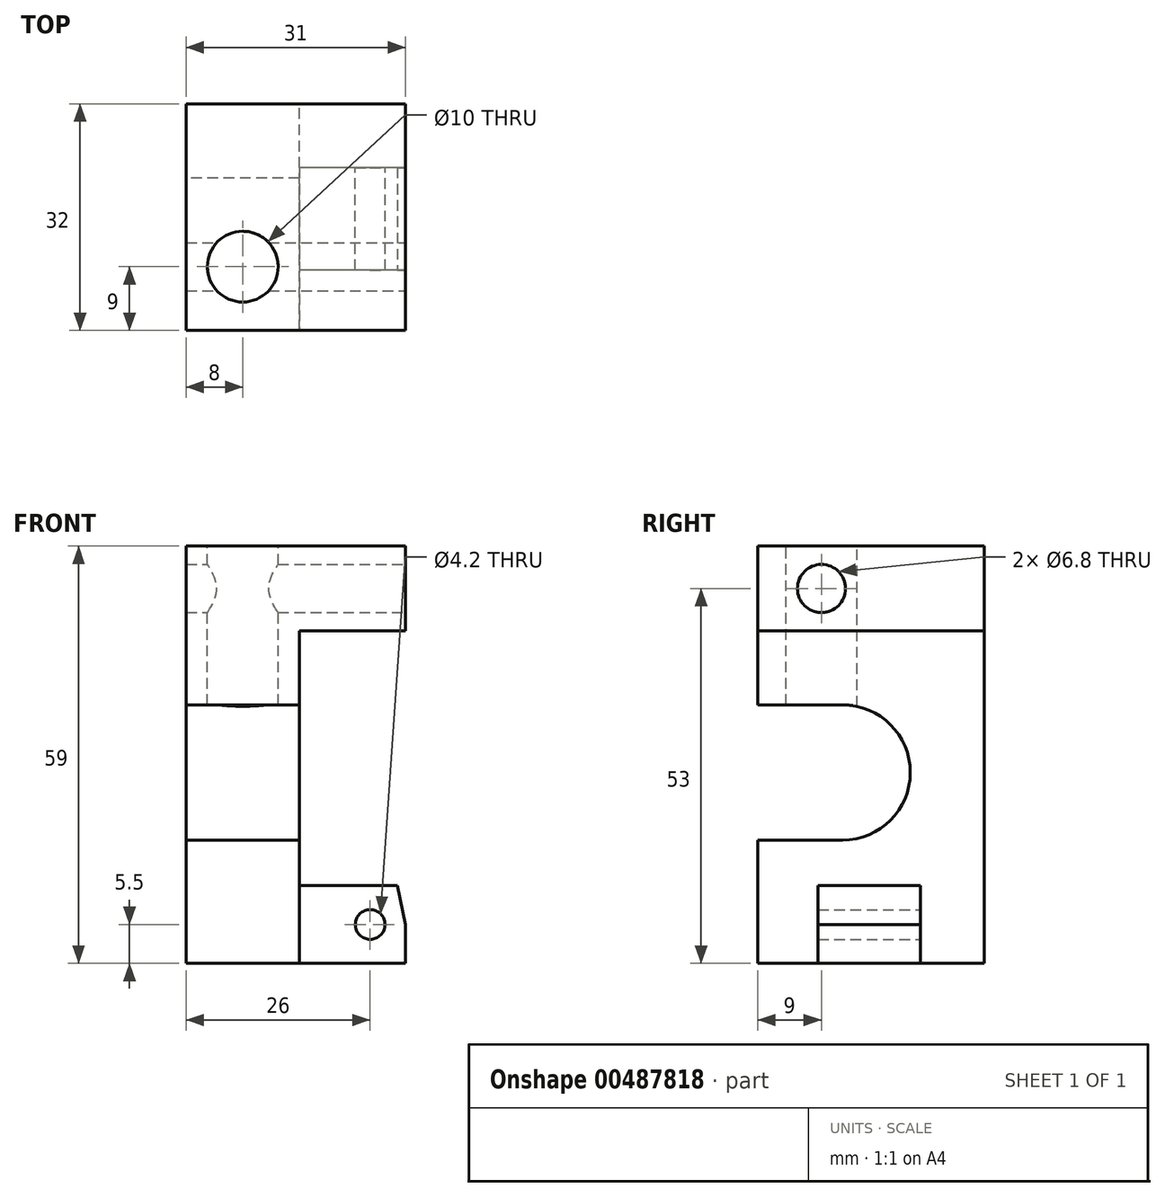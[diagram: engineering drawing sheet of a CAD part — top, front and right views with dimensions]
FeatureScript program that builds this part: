
annotation { "Feature Type Name" : "Feature", "Feature Type Description" : "" }
export const myFeature = defineFeature(function(context is Context, id is Id, definition is map)
    precondition{}
    {
        {
            var Q0;
            Q0=qCreatedBy(makeId("Right.planeOp"),FACE);
            var sketch = newSketch(context, id + "F0", { "sketchPlane" : qUnion([Q0])});
            skArc(sketch, "E0", {"start": v(0, -9.55) * mm, "mid": v(9.55, 0) * mm, "end": v(0, 9.55) * mm});
            skLineSegment(sketch, "E1.bottom", {"start": v(-12, 32) * mm, "end": v(20, 32) * mm});
            skLineSegment(sketch, "E1.top", {"start": v(-12, -27) * mm, "end": v(20, -27) * mm});
            skLineSegment(sketch, "E1.left", {"start": v(-12, 32) * mm, "end": v(-12, -27) * mm});
            skLineSegment(sketch, "E1.right", {"start": v(20, 32) * mm, "end": v(20, -27) * mm});
            skLineSegment(sketch, "E2.bottom", {"start": v(0, 9.55) * mm, "end": v(-12, 9.55) * mm});
            skLineSegment(sketch, "E2.top", {"start": v(0, -9.55) * mm, "end": v(-12, -9.55) * mm});
            skPoint(sketch, "E3.orphan", {"position": v(20, 9.55) * mm});
            skPoint(sketch, "E4.orphan", {"position": v(20, -9.55) * mm});
            skPoint(sketch, "E2.right.start.orphan", {"position": v(-20, 9.55) * mm});
            skPoint(sketch, "E5.orphan", {"position": v(-20, -9.55) * mm});
            skSolve(sketch);
        }
        {
            var Q0;
            Q0=makeQuery(id+"F0.imprint","IMPRINT",FACE,{"disambiguationData":[TD([[makeQuery(id+"F0.imprint","IMPRINT",EDGE,{"derivedFrom":sQuery(id+"F0.wireOp",EDGE,"E0")}),-1.0]])]});
            extrude(context, id + "F1", {"entities" : qUnion([Q0]), "depth" : 16 * mm, "offsetDistance" : 25 * mm});
        }
        {
            var Q0;
            Q0=makeQuery(id+"F1.opExtrude","CAP_FACE",FACE,{"disambiguationData":[OSD([sQuery(id+"F0.wireOp",EDGE,"E0"),sQuery(id+"F0.wireOp",EDGE,"E1.bottom"),sQuery(id+"F0.wireOp",EDGE,"E1.top"),sQuery(id+"F0.wireOp",EDGE,"E1.left"),sQuery(id+"F0.wireOp",EDGE,"E1.right")])],"isStart":false});
            var sketch = newSketch(context, id + "F2", { "sketchPlane" : qUnion([Q0])});
            skLineSegment(sketch, "E6.bottom", {"start": v(11, -27) * mm, "end": v(-3.5, -27) * mm});
            skLineSegment(sketch, "E6.top", {"start": v(11, -16) * mm, "end": v(-3.5, -16) * mm});
            skLineSegment(sketch, "E6.left", {"start": v(11, -27) * mm, "end": v(11, -16) * mm});
            skLineSegment(sketch, "E6.right", {"start": v(-3.5, -27) * mm, "end": v(-3.5, -16) * mm});
            skSolve(sketch);
        }
        {
            var Q0;
            Q0=makeQuery(id+"F2.imprint","IMPRINT",FACE,{"disambiguationData":[TD([[makeQuery(id+"F2.imprint","IMPRINT",EDGE,{"derivedFrom":sQuery(id+"F2.wireOp",EDGE,"E6.bottom")}),1.0]])]});
            extrude(context, id + "F3", {"entities" : qUnion([Q0]), "operationType" : NewBodyOperationType.ADD, "depth" : 15 * mm, "offsetDistance" : 25 * mm});
        }
        {
            var Q0;
            Q0=makeQuery(id+"F3.opExtrude","SWEPT_FACE",FACE,{"disambiguationData":[OSD([sQuery(id+"F2.wireOp",EDGE,"E6.right")])]});
            var sketch = newSketch(context, id + "F4", { "sketchPlane" : qUnion([Q0])});
            skLineSegment(sketch, "E7", {"start": v(31, -21.5) * mm, "end": v(31, -16) * mm});
            skLineSegment(sketch, "E8", {"start": v(31, -16) * mm, "end": v(29.83, -16) * mm});
            skLineSegment(sketch, "E9", {"start": v(29.83, -16) * mm, "end": v(31, -21.5) * mm});
            skSolve(sketch);
        }
        {
            var Q0;
            Q0=makeQuery(id+"F4.imprint","IMPRINT",FACE,{"disambiguationData":[TD([[makeQuery(id+"F4.imprint","IMPRINT",EDGE,{"derivedFrom":sQuery(id+"F4.wireOp",EDGE,"E7")}),1.0]])]});
            extrude(context, id + "F5", {"entities" : qUnion([Q0]), "operationType" : NewBodyOperationType.REMOVE, "endBound" : BoundingType.THROUGH_ALL, "oppositeDirection" : true, "depth" : 25 * mm, "offsetDistance" : 25 * mm});
        }
        {
            var Q0;
            Q0=makeQuery(id+"F3.opExtrude","SWEPT_FACE",FACE,{"disambiguationData":[OSD([sQuery(id+"F2.wireOp",EDGE,"E6.left")])]});
            var sketch = newSketch(context, id + "F6", { "sketchPlane" : qUnion([Q0])});
            skPoint(sketch, "E10", {"position": v(-26, -21.5) * mm});
            skSolve(sketch);
        }
        {
            var Q0;
            Q0=sQuery(id+"F6.wireOp",VERTEX,"E10");
            var Q1;
            Q1=makeQuery(id+"F1.opExtrude","SWEPT_BODY",BODY,{"disambiguationData":[OSD([sQuery(id+"F0.wireOp",EDGE,"E0"),sQuery(id+"F0.wireOp",EDGE,"E1.bottom"),sQuery(id+"F0.wireOp",EDGE,"E1.top"),sQuery(id+"F0.wireOp",EDGE,"E1.left"),sQuery(id+"F0.wireOp",EDGE,"E1.right"),sQuery(id+"F0.wireOp",EDGE,"E2.bottom"),sQuery(id+"F0.wireOp",EDGE,"E2.top")])]});
            hole(context, id + "F7", {"style" : HoleStyle.SIMPLE, "endStyle" : HoleEndStyle.THROUGH, "standardTappedOrClearance" : lookupTablePath({ "standard" : "ISO", "engagement" : "75%", "pitch" : "0.8 mm", "size" : "M5", "type" : "Tapped" }), "standardBlindInLast" : lookupTablePath({ "standard" : "ISO", "engagement" : "75%", "pitch" : "0.8 mm", "size" : "M5", "type" : "Tapped" }), "holeDiameter" : 4.2 * mm, "showTappedDepth" : true, "isTappedThrough" : true, "tappedDepth" : 12 * mm, "tapClearance" : 3, "locations" : qUnion([Q0]), "scope" : qUnion([Q1]), "majorDiameter" : 5 * mm});
        }
        {
            var Q0;
            Q0=makeQuery(id+"F1.opExtrude","CAP_FACE",FACE,{"disambiguationData":[OSD([sQuery(id+"F0.wireOp",EDGE,"E0"),sQuery(id+"F0.wireOp",EDGE,"E1.bottom"),sQuery(id+"F0.wireOp",EDGE,"E1.top"),sQuery(id+"F0.wireOp",EDGE,"E1.left"),sQuery(id+"F0.wireOp",EDGE,"E1.right"),sQuery(id+"F0.wireOp",EDGE,"E2.bottom"),sQuery(id+"F0.wireOp",EDGE,"E2.top")])],"isStart":false});
            var sketch = newSketch(context, id + "F8", { "sketchPlane" : qUnion([Q0])});
            skLineSegment(sketch, "E11.bottom", {"start": v(-12, 32) * mm, "end": v(20, 32) * mm});
            skLineSegment(sketch, "E11.top", {"start": v(-12, 20) * mm, "end": v(20, 20) * mm});
            skLineSegment(sketch, "E11.left", {"start": v(-12, 32) * mm, "end": v(-12, 20) * mm});
            skLineSegment(sketch, "E11.right", {"start": v(20, 32) * mm, "end": v(20, 20) * mm});
            skSolve(sketch);
        }
        {
            var Q0;
            Q0=makeQuery(id+"F8.imprint","IMPRINT",FACE,{"disambiguationData":[TD([[makeQuery(id+"F8.imprint","IMPRINT",EDGE,{"derivedFrom":sQuery(id+"F8.wireOp",EDGE,"E11.bottom")}),-1.0]])]});
            extrude(context, id + "F9", {"entities" : qUnion([Q0]), "operationType" : NewBodyOperationType.ADD, "depth" : 15 * mm, "offsetDistance" : 25 * mm});
        }
        {
            var Q0;
            Q0=makeQuery(id+"F9.boolean.opBoolean","MERGE",FACE,{"derivedFrom":[makeQuery(id+"F1.opExtrude","SWEPT_FACE",FACE,{"disambiguationData":[OSD([sQuery(id+"F0.wireOp",EDGE,"E1.bottom")])]}),makeQuery(id+"F9.opExtrude","SWEPT_FACE",FACE,{"disambiguationData":[OSD([sQuery(id+"F8.wireOp",EDGE,"E11.bottom")])]})]});
            var sketch = newSketch(context, id + "F10", { "sketchPlane" : qUnion([Q0])});
            skCircle(sketch, "E12", {"center": v(8, -3) * mm, "radius": 5 * mm});
            skSolve(sketch);
        }
        {
            var Q0;
            Q0=makeQuery(id+"F10.imprint","IMPRINT",FACE,{"disambiguationData":[TD([[makeQuery(id+"F10.imprint","IMPRINT",EDGE,{"derivedFrom":sQuery(id+"F10.wireOp",EDGE,"E12")}),1.0]])]});
            extrude(context, id + "F11", {"entities" : qUnion([Q0]), "operationType" : NewBodyOperationType.REMOVE, "oppositeDirection" : true, "depth" : 25 * mm, "offsetDistance" : 25 * mm});
        }
        {
            var Q0;
            Q0=makeQuery(id+"F9.opExtrude","CAP_FACE",FACE,{"disambiguationData":[OSD([sQuery(id+"F8.wireOp",EDGE,"E11.bottom"),sQuery(id+"F8.wireOp",EDGE,"E11.top"),sQuery(id+"F8.wireOp",EDGE,"E11.left"),sQuery(id+"F8.wireOp",EDGE,"E11.right")])],"isStart":false});
            var sketch = newSketch(context, id + "F12", { "sketchPlane" : qUnion([Q0])});
            skPoint(sketch, "E13", {"position": v(-3, 26) * mm});
            skSolve(sketch);
        }
        {
            var Q0;
            Q0=sQuery(id+"F12.wireOp",VERTEX,"E13");
            var Q1;
            Q1=makeQuery(id+"F1.opExtrude","SWEPT_BODY",BODY,{"disambiguationData":[OSD([sQuery(id+"F0.wireOp",EDGE,"E0"),sQuery(id+"F0.wireOp",EDGE,"E1.bottom"),sQuery(id+"F0.wireOp",EDGE,"E1.top"),sQuery(id+"F0.wireOp",EDGE,"E1.left"),sQuery(id+"F0.wireOp",EDGE,"E1.right"),sQuery(id+"F0.wireOp",EDGE,"E2.bottom"),sQuery(id+"F0.wireOp",EDGE,"E2.top")])]});
            hole(context, id + "F13", {"style" : HoleStyle.SIMPLE, "endStyle" : HoleEndStyle.THROUGH, "standardTappedOrClearance" : lookupTablePath({ "standard" : "ISO", "engagement" : "75%", "pitch" : "1.25 mm", "size" : "M8", "type" : "Tapped" }), "standardBlindInLast" : lookupTablePath({ "standard" : "ISO", "engagement" : "75%", "pitch" : "1.25 mm", "size" : "M8", "type" : "Tapped" }), "holeDiameter" : 6.8 * mm, "majorDiameter" : 8 * mm, "showTappedDepth" : true, "isTappedThrough" : true, "tappedDepth" : 12 * mm, "tapClearance" : 3, "locations" : qUnion([Q0]), "scope" : qUnion([Q1])});
        }
    });
